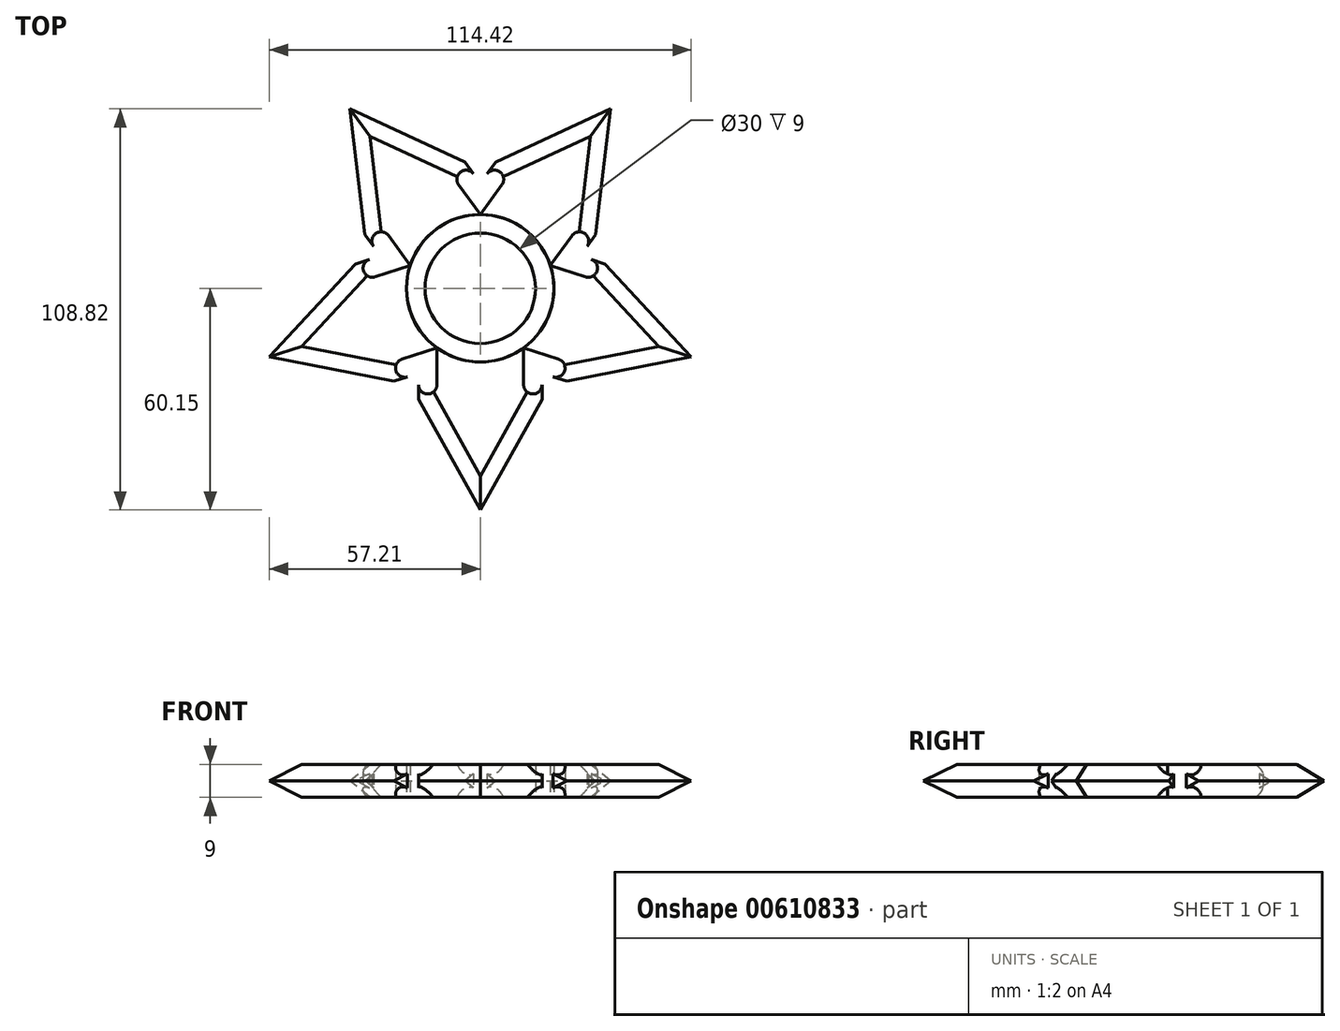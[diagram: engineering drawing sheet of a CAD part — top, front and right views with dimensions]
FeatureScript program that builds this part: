
annotation { "Feature Type Name" : "Feature", "Feature Type Description" : "" }
export const myFeature = defineFeature(function(context is Context, id is Id, definition is map)
    precondition{}
    {
        {
            var Q0;
            Q0=qCreatedBy(makeId("Top.planeOp"),FACE);
            var sketch = newSketch(context, id + "F0", { "sketchPlane" : qUnion([Q0])});
            skCircle(sketch, "E0", {"center": v(0, 0) * mm, "radius": 15 * mm});
            skCircle(sketch, "E1", {"center": v(0, 0) * mm, "radius": 20 * mm});
            skCircle(sketch, "E2.cCircle", {"center": v(0, 0) * mm, "radius": 20 * mm, "construction": true});
            skSolve(sketch);
        }
        {
            var Q0;
            Q0=makeQuery(id+"F0.imprint","IMPRINT",FACE,{"disambiguationData":[TD([[makeQuery(id+"F0.imprint","IMPRINT",EDGE,{"derivedFrom":sQuery(id+"F0.wireOp",EDGE,"E0")}),-1.0]])]});
            extrude(context, id + "F1", {"entities" : qUnion([Q0]), "depth" : 9 * mm, "offsetDistance" : 25 * mm});
        }
        {
            var Q0;
            Q0=makeQuery(id+"F1.opExtrude","CAP_FACE",FACE,{"disambiguationData":[OSD([sQuery(id+"F0.wireOp",EDGE,"E0"),sQuery(id+"F0.wireOp",EDGE,"E1")])],"isStart":true});
            var sketch = newSketch(context, id + "F2", { "sketchPlane" : qUnion([Q0])});
            skLineSegment(sketch, "E3.0", {"start": v(0, -20) * mm, "end": v(-19.02, -6.18) * mm});
            skLineSegment(sketch, "E3.1", {"start": v(-19.02, -6.18) * mm, "end": v(-11.76, 16.18) * mm});
            skLineSegment(sketch, "E3.2", {"start": v(-11.76, 16.18) * mm, "end": v(11.76, 16.18) * mm});
            skLineSegment(sketch, "E3.3", {"start": v(11.76, 16.18) * mm, "end": v(19.02, -6.18) * mm});
            skLineSegment(sketch, "E3.4", {"start": v(19.02, -6.18) * mm, "end": v(0, -20) * mm});
            skLineSegment(sketch, "E4", {"start": v(0, -20) * mm, "end": v(5.88, -28.1) * mm});
            skLineSegment(sketch, "E5", {"start": v(5.88, -28.1) * mm, "end": v(1.83, -31.03) * mm});
            skLineSegment(sketch, "E6", {"start": v(19.02, -6.18) * mm, "end": v(24.9, -14.27) * mm});
            skLineSegment(sketch, "E7", {"start": v(24.9, -14.27) * mm, "end": v(28.94, -11.33) * mm});
            skCircle(sketch, "E8", {"center": v(3.86, -29.56) * mm, "radius": 2.5 * mm});
            skCircle(sketch, "E9", {"center": v(26.92, -12.8) * mm, "radius": 2.5 * mm});
            skLineSegment(sketch, "E10", {"start": v(1.83, -31.03) * mm, "end": v(4.77, -35.07) * mm});
            skLineSegment(sketch, "E11", {"start": v(28.94, -11.33) * mm, "end": v(31.88, -15.38) * mm});
            skLineSegment(sketch, "E12", {"start": v(4.77, -35.07) * mm, "end": v(35.96, -49.5) * mm});
            skLineSegment(sketch, "E13", {"start": v(31.88, -15.38) * mm, "end": v(35.96, -49.5) * mm});
            skSolve(sketch);
        }
        {
            var Q0;
            {var subQ6=sQuery(id+"F2.wireOp",EDGE,"E4");Q0=makeQuery(id+"F2.imprint","IMPRINT",FACE,{"disambiguationData":[TD([[makeQuery(id+"F2.imprint","IMPRINT",EDGE,{"derivedFrom":subQ6}),1.0]])]});}
            extrude(context, id + "F3", {"entities" : qUnion([Q0]), "oppositeDirection" : true, "depth" : 9 * mm, "offsetDistance" : 25 * mm});
        }
        {
            var Q0;
            Q0=makeQuery(id+"F3.opExtrude","CAP_EDGE",EDGE,{"disambiguationData":[OSD([sQuery(id+"F2.wireOp",EDGE,"E13")])],"isStart":false});
            var Q1;
            Q1=makeQuery(id+"F3.opExtrude","CAP_EDGE",EDGE,{"disambiguationData":[OSD([sQuery(id+"F2.wireOp",EDGE,"E12")])],"isStart":false});
            chamfer(context, id + "F4", {"entities" : qUnion([Q0, Q1]), "width" : 5 * mm, "tangentPropagation" : true});
        }
        {
            var Q0;
            Q0=makeQuery(id+"F3.opExtrude","CAP_EDGE",EDGE,{"disambiguationData":[OSD([sQuery(id+"F2.wireOp",EDGE,"E13")])],"isStart":true});
            var Q1;
            Q1=makeQuery(id+"F3.opExtrude","CAP_EDGE",EDGE,{"disambiguationData":[OSD([sQuery(id+"F2.wireOp",EDGE,"E12")])],"isStart":true});
            chamfer(context, id + "F5", {"entities" : qUnion([Q0, Q1]), "width" : 5 * mm, "tangentPropagation" : true});
        }
        {
            var Q0;
            Q0=makeQuery(id+"F3.opExtrude","SWEPT_BODY",BODY,{"disambiguationData":[OSD([sQuery(id+"F0.wireOp",EDGE,"E1"),sQuery(id+"F2.wireOp",EDGE,"E4"),sQuery(id+"F2.wireOp",EDGE,"E6"),sQuery(id+"F2.wireOp",EDGE,"E8"),sQuery(id+"F2.wireOp",EDGE,"E9"),sQuery(id+"F2.wireOp",EDGE,"E10"),sQuery(id+"F2.wireOp",EDGE,"E11"),sQuery(id+"F2.wireOp",EDGE,"E12"),sQuery(id+"F2.wireOp",EDGE,"E13")])]});
            var Q1;
            Q1=makeQuery(id+"F1.opExtrude","CAP_EDGE",EDGE,{"disambiguationData":[OSD([sQuery(id+"F0.wireOp",EDGE,"E1")])],"isStart":false});
            circularPattern(context, id + "F6", {"entities" : qUnion([Q0]), "axis" : qUnion([Q1]), "angle" : 360 * degree, "instanceCount" : 5, "equalSpace" : true});
        }
    });
